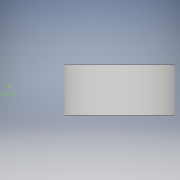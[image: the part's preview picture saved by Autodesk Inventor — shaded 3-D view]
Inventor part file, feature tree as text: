
AUTODESK INVENTOR PART (.ipt)
format: ipt  version: 2018 (Build 220112000, 112)  size: 274,944 bytes
history: native  units: in
note: dims shown in document units (in); Inventor stores cm internally (conversion verified against a paired STEP export)
features: sketch x2, revolve x1
ambient origin geometry x8: Origin, YZ Plane, XZ Plane, XY Plane, X Axis, Y Axis, Z Axis, Center Point
bodies: Solid1 (feature_tree)
feature tree (3):
  revolve  "Revolution1"  [1 undecoded]
  sketch  "Sketch18"  dims[d2=90.0deg d14=0.5828in d119=0.3622in d133=0.3622in d149=0.3622in d160=0.3622in d170=0.0118in d176=0.0118in d180=0.3622in d181=0.0118in]
  sketch  "Sketch1"  dims[d0=0.3963in d1=0.3739in]
note: 1 required parameter value undecoded (feature->parameter linkage not recoverable at this tier; creation-order binding heuristic only, values carry confidence <= 0.55)
